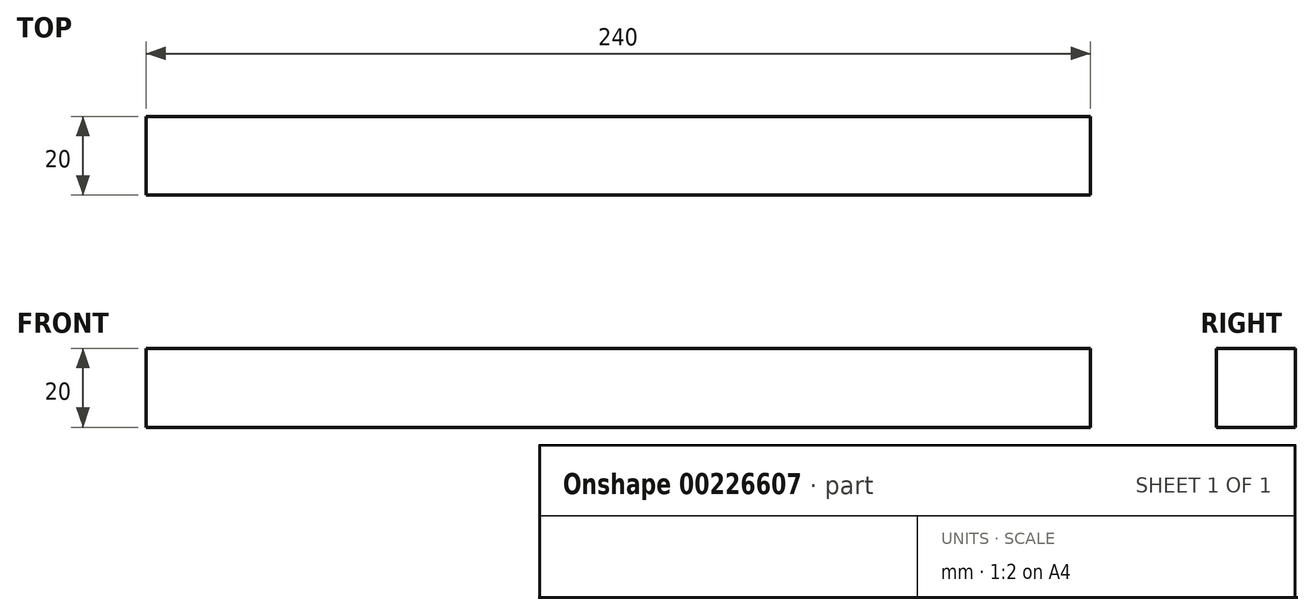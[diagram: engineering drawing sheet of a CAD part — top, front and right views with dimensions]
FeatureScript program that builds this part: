
annotation { "Feature Type Name" : "Feature", "Feature Type Description" : "" }
export const myFeature = defineFeature(function(context is Context, id is Id, definition is map)
    precondition{}
    {
        {
            var Q0;
            Q0=qCreatedBy(makeId("Top.planeOp"),FACE);
            var sketch = newSketch(context, id + "F0", { "sketchPlane" : qUnion([Q0])});
            skLineSegment(sketch, "E0.bottom", {"start": v(-120, 10) * mm, "end": v(120, 10) * mm});
            skLineSegment(sketch, "E0.top", {"start": v(-120, -10) * mm, "end": v(120, -10) * mm});
            skLineSegment(sketch, "E0.left", {"start": v(-120, 10) * mm, "end": v(-120, -10) * mm});
            skLineSegment(sketch, "E0.right", {"start": v(120, 10) * mm, "end": v(120, -10) * mm});
            skLineSegment(sketch, "E1", {"start": v(-120, -10) * mm, "end": v(120, 10) * mm, "construction": true});
            skLineSegment(sketch, "E2", {"start": v(-120, 10) * mm, "end": v(120, -10) * mm, "construction": true});
            skSolve(sketch);
        }
        {
            var Q0;
            Q0=qSketchRegion(id+"F0",true);
            extrude(context, id + "F1", {"entities" : qUnion([Q0]), "depth" : 20 * mm});
        }
    });
